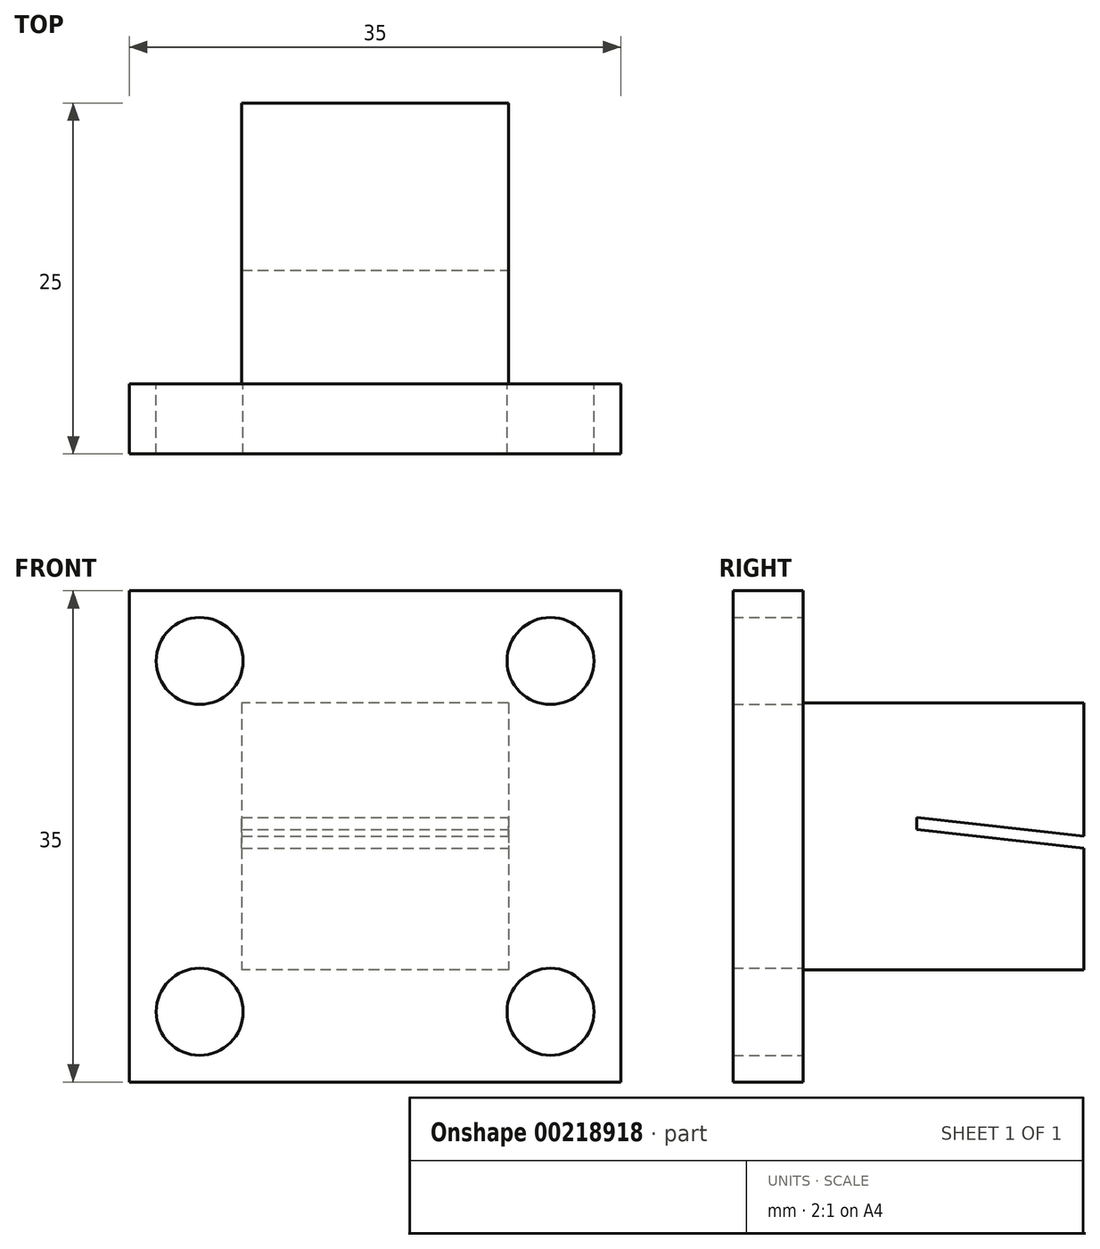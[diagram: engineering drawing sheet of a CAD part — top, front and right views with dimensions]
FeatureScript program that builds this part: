
annotation { "Feature Type Name" : "Feature", "Feature Type Description" : "" }
export const myFeature = defineFeature(function(context is Context, id is Id, definition is map)
    precondition{}
    {
        {
            var Q0;
            Q0=qCreatedBy(makeId("Front.planeOp"),FACE);
            var sketch = newSketch(context, id + "F0", { "sketchPlane" : qUnion([Q0])});
            skLineSegment(sketch, "E0.bottom", {"start": v(-16.94, 0) * mm, "end": v(18.06, 0) * mm});
            skLineSegment(sketch, "E0.top", {"start": v(-16.94, -35) * mm, "end": v(18.06, -35) * mm});
            skLineSegment(sketch, "E0.left", {"start": v(-16.94, 0) * mm, "end": v(-16.94, -35) * mm});
            skLineSegment(sketch, "E0.right", {"start": v(18.06, 0) * mm, "end": v(18.06, -35) * mm});
            skSolve(sketch);
        }
        {
            var Q0;
            Q0=qSketchRegion(id+"F0",true);
            extrude(context, id + "F1", {"entities" : qUnion([Q0]), "depth" : 5 * mm});
        }
        {
            var Q0;
            Q0=makeQuery(id+"F1.opExtrude","CAP_FACE",FACE,{"disambiguationData":[OSD([sQuery(id+"F0.wireOp",EDGE,"E0.bottom"),sQuery(id+"F0.wireOp",EDGE,"E0.top"),sQuery(id+"F0.wireOp",EDGE,"E0.left"),sQuery(id+"F0.wireOp",EDGE,"E0.right")])],"isStart":true});
            var sketch = newSketch(context, id + "F2", { "sketchPlane" : qUnion([Q0])});
            skCircle(sketch, "E1", {"center": v(-13.06, -5) * mm, "radius": 3.1 * mm});
            skLineSegment(sketch, "E2", {"start": v(-18.06, -17.5) * mm, "end": v(16.94, -17.5) * mm});
            skCircle(sketch, "E3", {"center": v(11.94, -5) * mm, "radius": 3.1 * mm});
            skLineSegment(sketch, "E4", {"start": v(-0.56, -35) * mm, "end": v(-0.56, 0) * mm});
            skCircle(sketch, "E5", {"center": v(-13.06, -30) * mm, "radius": 3.1 * mm});
            skCircle(sketch, "E6", {"center": v(11.94, -30) * mm, "radius": 3.1 * mm});
            skSolve(sketch);
        }
        {
            var Q0;
            Q0=qSketchRegion(id+"F2",true);
            extrude(context, id + "F3", {"entities" : qUnion([Q0]), "operationType" : NewBodyOperationType.REMOVE, "endBound" : BoundingType.THROUGH_ALL, "oppositeDirection" : true, "depth" : 25 * mm});
        }
        {
            var Q0;
            Q0=makeQuery(id+"F1.opExtrude","CAP_FACE",FACE,{"disambiguationData":[OSD([sQuery(id+"F0.wireOp",EDGE,"E0.bottom"),sQuery(id+"F0.wireOp",EDGE,"E0.top"),sQuery(id+"F0.wireOp",EDGE,"E0.left"),sQuery(id+"F0.wireOp",EDGE,"E0.right")])],"isStart":true});
            var sketch = newSketch(context, id + "F4", { "sketchPlane" : qUnion([Q0])});
            skLineSegment(sketch, "E7.bottom", {"start": v(-10.06, -8) * mm, "end": v(8.94, -8) * mm});
            skLineSegment(sketch, "E7.top", {"start": v(-10.06, -27) * mm, "end": v(8.94, -27) * mm});
            skLineSegment(sketch, "E7.left", {"start": v(-10.06, -8) * mm, "end": v(-10.06, -27) * mm});
            skLineSegment(sketch, "E7.right", {"start": v(8.94, -8) * mm, "end": v(8.94, -27) * mm});
            skSolve(sketch);
        }
        {
            var Q0;
            Q0=makeQuery(id+"F4.imprint","IMPRINT",FACE,{"disambiguationData":[TD([[makeQuery(id+"F4.imprint","IMPRINT",EDGE,{"derivedFrom":sQuery(id+"F4.wireOp",EDGE,"E7.bottom")}),-1.0]])]});
            extrude(context, id + "F5", {"entities" : qUnion([Q0]), "operationType" : NewBodyOperationType.ADD, "depth" : 20 * mm, "offsetDistance" : 25 * mm});
        }
        {
            var Q0;
            Q0=makeQuery(id+"F5.opExtrude","SWEPT_FACE",FACE,{"disambiguationData":[OSD([sQuery(id+"F4.wireOp",EDGE,"E7.left")])]});
            var sketch = newSketch(context, id + "F6", { "sketchPlane" : qUnion([Q0])});
            skLineSegment(sketch, "E8", {"start": v(20, -17.5) * mm, "end": v(8.08, -16.15) * mm});
            skLineSegment(sketch, "E9", {"start": v(8.08, -17) * mm, "end": v(20, -18.36) * mm});
            skPoint(sketch, "E9.startSnap0", {"position": v(14.04, -16.82) * mm});
            skLineSegment(sketch, "E10", {"start": v(20, -17.5) * mm, "end": v(20, -18.36) * mm});
            skLineSegment(sketch, "E11", {"start": v(8.08, -16.15) * mm, "end": v(8.08, -17) * mm});
            skPoint(sketch, "E12.orphan", {"position": v(6.5, -16.82) * mm});
            skSolve(sketch);
        }
        {
            var Q0;
            Q0 = qSketchRegion(id + "F6", true);
            extrude(context, id + "F7", {"entities" : qUnion([Q0]), "operationType" : NewBodyOperationType.REMOVE, "oppositeDirection" : true, "depth" : 35 * mm, "offsetDistance" : 25 * mm});
        }
    });
